# Revit family: Shower_System-Grohe-Euphoria-26128_Series
name_source: partatom
category: Plumbing Fixtures
revit_build: Autodesk Revit 2018 (Build: 20170223_1515(x64)
units: mm (PartAtom-declared; Revit-internal decimal feet)

## family parameters
Cut with Voids When Loaded = No
Host = Face
OmniClass Number = 23.45.05.14.17
OmniClass Title = Showers
Part Type = Normal
Room Calculation Point = No
Round Connector Dimension = Use Diameter
Shared = Yes

## types (4) — shared parameters
Assembly Code = D2010710
CW Connection = Yes
CWFU = 3
Cold Water Connection Diameter = 1/2"
Default Elevation = 0"
Description = EUPHORIA SYSTEM 260 Shower System with Thermostat for Wall Mount
HW Connection = Yes
HWFU = 3
Height = 0"
Hot Water Connection Diameter = 1/2"
Installation Type = Wall Mounted
Manufacturer = Grohe
Price = Prices may vary. Please consult Manufacturer Representative for most up-to-date price list.
Product Documentation Link = https://americanstandard.box.com
Product Page URL = https://www.grohe.us
URL = https://www.grohe.us
Vent Connection = No
WFU = 4
Warranty Information = Limited Lifetime Warranty
Waste Connection = No
Width = 18 1/4"

## per-type parameters (varying)
| type | Finish | Flow Rate | Length | Material | Shower Head Width |
| 26128002 | Metal-Grohe-002-Chrome | 1.75 gpm (6.6 l/min) | 12 1/8" | Metal-Grohe-002-Chrome | 0" |
| 26128001 | Metal-Grohe-001-Chrome | 2.5 gpm (9.5 l/min) | 11 3/4" | Metal-Grohe-001-Chrome | 30" |
| 26128EN1 | Metal-Grohe-EN1-Brushed Nickel Infinity Finish | 2.5 gpm (9.5 l/min) | 11 3/4" | Metal-Grohe-EN1-Brushed Nickel Infinity Finish | 30" |
| 26128EN2 | Metal-Grohe-000-Chrome | 1.75 gpm (6.6 l/min) | 12 1/8" | Metal-Grohe-EN2-Brushed Nickel Infinity Finish | 0" |

note: column(s) folded — value = type name in every type: Model

## geometry (parser evidence)
native form markers: Sweep x2
no freeform markers — native parametric forms only
